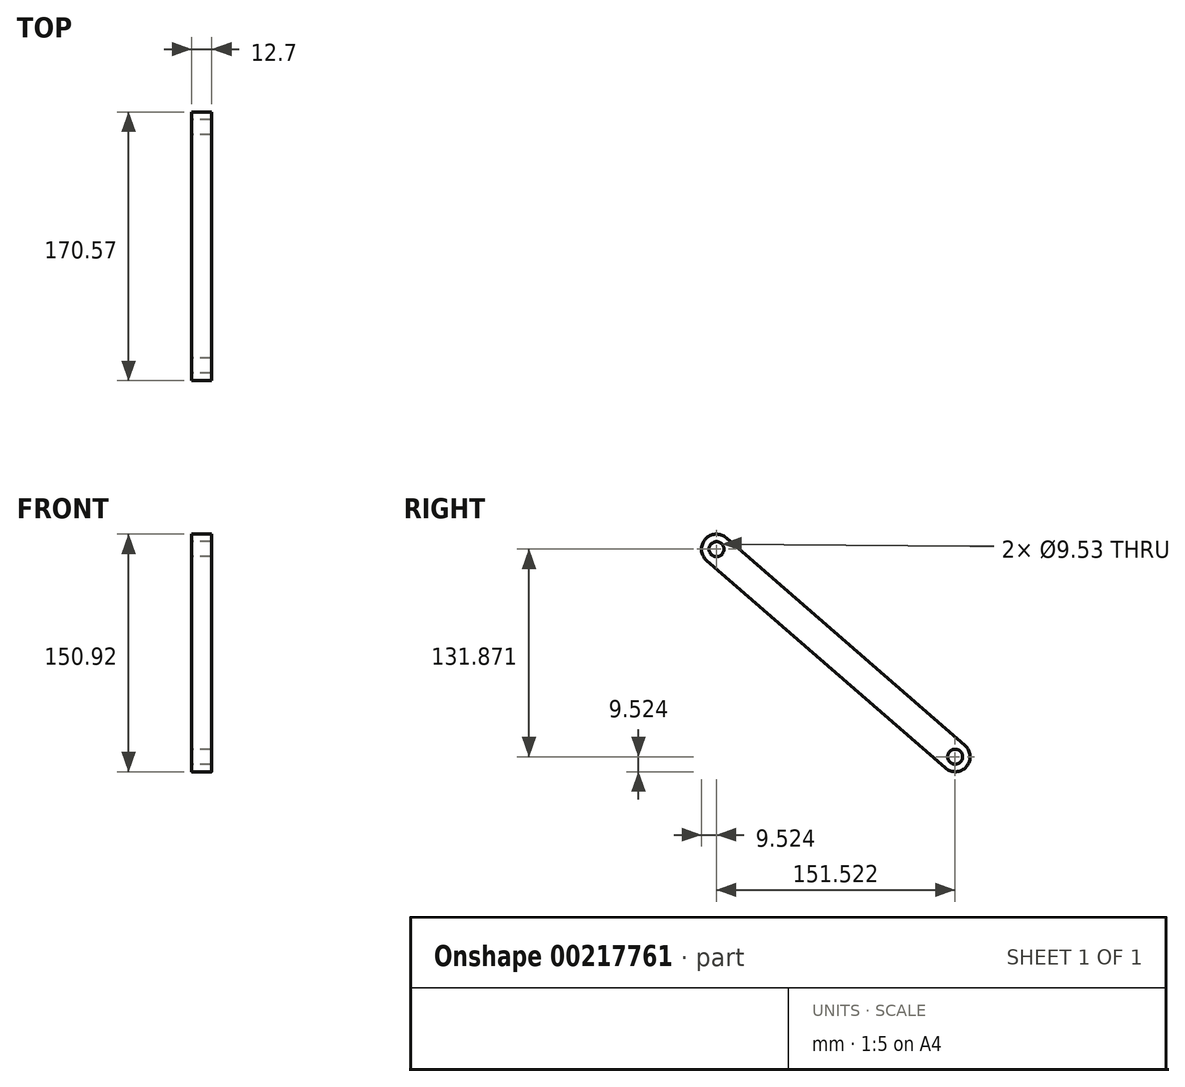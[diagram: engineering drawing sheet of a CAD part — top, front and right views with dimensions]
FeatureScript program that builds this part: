
annotation { "Feature Type Name" : "Feature", "Feature Type Description" : "" }
export const myFeature = defineFeature(function(context is Context, id is Id, definition is map)
    precondition{}
    {
        {
            var Q0;
            Q0=qCreatedBy(makeId("Right.planeOp"),FACE);
            var sketch = newSketch(context, id + "F0", { "sketchPlane" : qUnion([Q0])});
            skCircle(sketch, "E0", {"center": v(141.35, 145.98) * mm, "radius": 9.53 * mm});
            skCircle(sketch, "E1", {"center": v(141.35, 145.98) * mm, "radius": 4.76 * mm});
            skLineSegment(sketch, "E2", {"start": v(147.6, 153.17) * mm, "end": v(-3.92, 285.04) * mm});
            skLineSegment(sketch, "E3", {"start": v(135.1, 138.8) * mm, "end": v(-16.43, 270.67) * mm});
            skCircle(sketch, "E4", {"center": v(-10.18, 277.86) * mm, "radius": 4.76 * mm});
            skCircle(sketch, "E5", {"center": v(-10.18, 277.86) * mm, "radius": 9.53 * mm});
            skSolve(sketch);
        }
        {
            var Q0;
            {var subQ5=sQuery(id+"F0.wireOp",EDGE,"E2");Q0=makeQuery(id+"F0.imprint","IMPRINT",FACE,{"disambiguationData":[TD([[makeQuery(id+"F0.imprint","IMPRINT",EDGE,{"derivedFrom":subQ5}),1.0]])]});}
            var Q1;
            Q1=makeQuery(id+"F0.imprint","IMPRINT",FACE,{"disambiguationData":[TD([[makeQuery(id+"F0.imprint","IMPRINT",EDGE,{"derivedFrom":sQuery(id+"F0.wireOp",EDGE,"E4")}),-1.0]])]});
            var Q2;
            {var subQ0=sQuery(id+"F0.wireOp",EDGE,"E0");var subQ1=sQuery(id+"F0.wireOp",EDGE,"rAX7Bpbj-aBWN-dt8I-5IVV-6u9TD1hBe2ji");var subQ2=makeQuery(id+"F0.imprint","INTERSECT",VERTEX,{"derivedFrom":[subQ1,subQ0]});Q2=makeQuery(id+"F0.imprint","IMPRINT",FACE,{"disambiguationData":[TD([[makeQuery(id+"F0.imprint","IMPRINT",EDGE,{"disambiguationData":[TD([[subQ2,1.0]])],"derivedFrom":subQ1}),-1.0]])]});}
            var Q3;
            Q3=makeQuery(id+"F0.imprint","IMPRINT",FACE,{"disambiguationData":[TD([[makeQuery(id+"F0.imprint","IMPRINT",EDGE,{"derivedFrom":sQuery(id+"F0.wireOp",EDGE,"E1")}),-1.0]])]});
            extrude(context, id + "F1", {"entities" : qUnion([Q0, Q1, Q2, Q3]), "depth" : 12.7 * mm});
        }
    });
